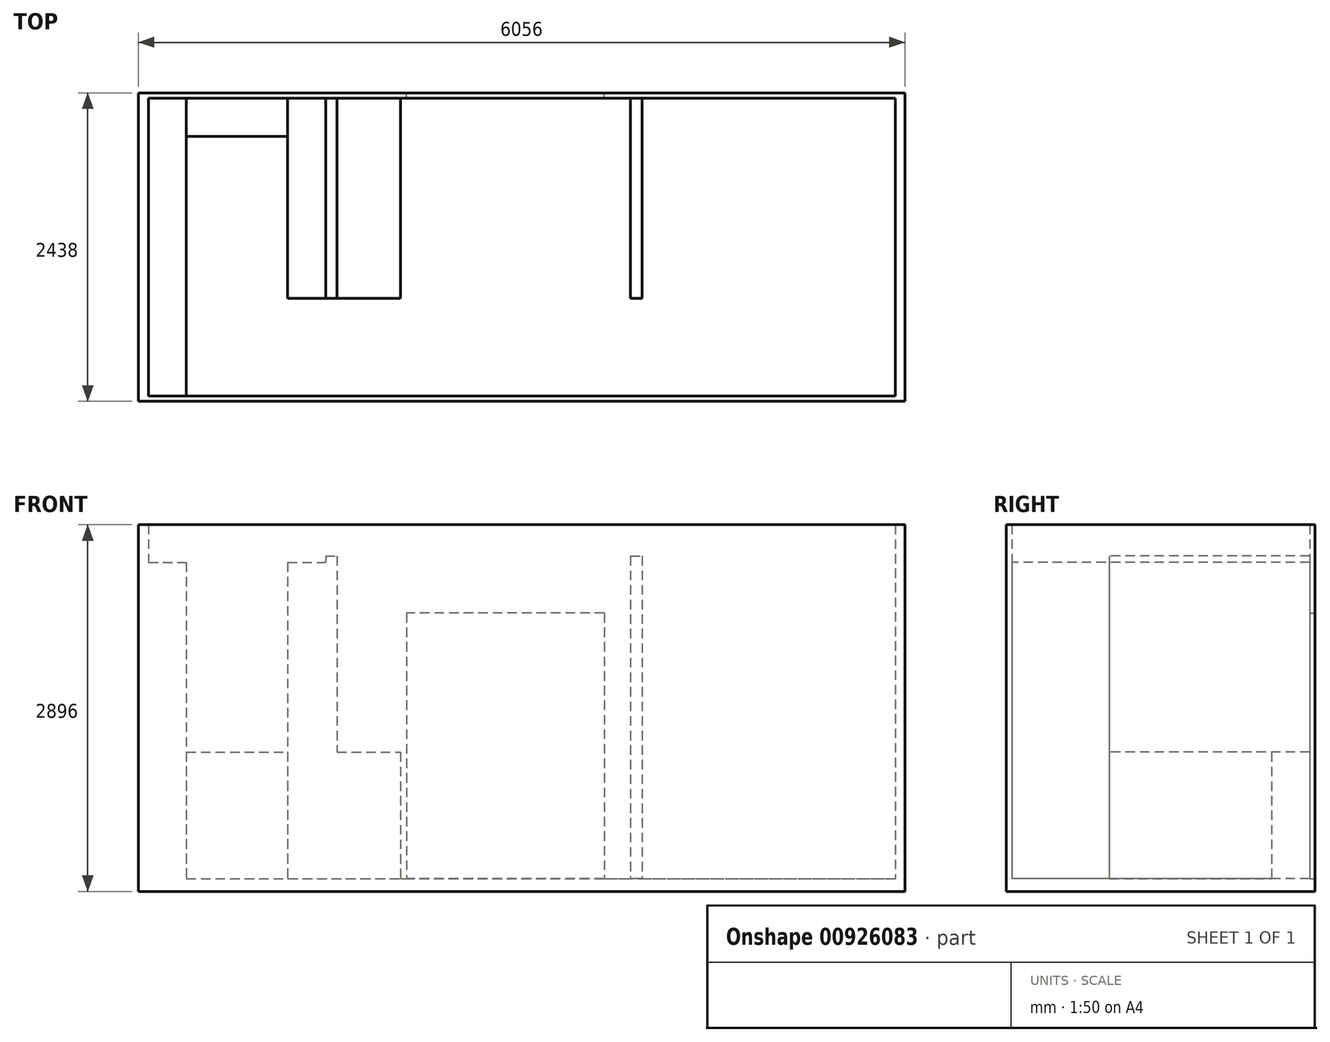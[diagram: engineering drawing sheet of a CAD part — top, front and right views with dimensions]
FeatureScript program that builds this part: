
annotation { "Feature Type Name" : "Feature", "Feature Type Description" : "" }
export const myFeature = defineFeature(function(context is Context, id is Id, definition is map)
    precondition{}
    {
        {
            var Q0;
            Q0=qCreatedBy(makeId("Top.planeOp"),FACE);
            var sketch = newSketch(context, id + "F0", { "sketchPlane" : qUnion([Q0])});
            skLineSegment(sketch, "E0.bottom", {"start": v(-2949, 1176) * mm, "end": v(2949, 1176) * mm});
            skLineSegment(sketch, "E0.top", {"start": v(-2949, -1176) * mm, "end": v(2949, -1176) * mm});
            skLineSegment(sketch, "E0.left", {"start": v(-2949, 1176) * mm, "end": v(-2949, -1176) * mm});
            skLineSegment(sketch, "E0.right", {"start": v(2949, 1176) * mm, "end": v(2949, -1176) * mm});
            skLineSegment(sketch, "E1.bottom", {"start": v(-3028, 1219) * mm, "end": v(3028, 1219) * mm});
            skLineSegment(sketch, "E1.top", {"start": v(-3028, -1219) * mm, "end": v(3028, -1219) * mm});
            skLineSegment(sketch, "E1.left", {"start": v(-3028, 1219) * mm, "end": v(-3028, -1219) * mm});
            skLineSegment(sketch, "E1.right", {"start": v(3028, 1219) * mm, "end": v(3028, -1219) * mm});
            skSolve(sketch);
        }
        {
            var Q0;
            Q0=makeQuery(id+"F0.imprint","IMPRINT",FACE,{"disambiguationData":[TD([[makeQuery(id+"F0.imprint","IMPRINT",EDGE,{"derivedFrom":sQuery(id+"F0.wireOp",EDGE,"E0.bottom")}),1.0]])]});
            extrude(context, id + "F1", {"entities" : qUnion([Q0]), "depth" : 2896 * mm, "offsetDistance" : 25 * mm});
        }
        {
            var Q0;
            Q0=makeQuery(id+"F0.imprint","IMPRINT",FACE,{"disambiguationData":[TD([[makeQuery(id+"F0.imprint","IMPRINT",EDGE,{"derivedFrom":sQuery(id+"F0.wireOp",EDGE,"E0.bottom")}),-1.0]])]});
            extrude(context, id + "F2", {"entities" : qUnion([Q0]), "operationType" : NewBodyOperationType.ADD, "depth" : 99 * mm, "offsetDistance" : 25 * mm});
        }
        {
            var Q0;
            Q0=makeQuery(id+"F2.opExtrude","CAP_FACE",FACE,{"disambiguationData":[OSD([sQuery(id+"F0.wireOp",EDGE,"E0.bottom"),sQuery(id+"F0.wireOp",EDGE,"E0.top"),sQuery(id+"F0.wireOp",EDGE,"E0.left"),sQuery(id+"F0.wireOp",EDGE,"E0.right")])],"isStart":false});
            var sketch = newSketch(context, id + "F3", { "sketchPlane" : qUnion([Q0])});
            skLineSegment(sketch, "E2.bottom", {"start": v(949, 1176) * mm, "end": v(859, 1176) * mm});
            skLineSegment(sketch, "E2.top", {"start": v(949, -406) * mm, "end": v(859, -406) * mm});
            skLineSegment(sketch, "E2.left", {"start": v(949, 1176) * mm, "end": v(949, -406) * mm});
            skLineSegment(sketch, "E2.right", {"start": v(859, 1176) * mm, "end": v(859, -406) * mm});
            skLineSegment(sketch, "E3.bottom", {"start": v(-1549, 1176) * mm, "end": v(-1459, 1176) * mm});
            skLineSegment(sketch, "E3.top", {"start": v(-1549, -406) * mm, "end": v(-1459, -406) * mm});
            skLineSegment(sketch, "E3.left", {"start": v(-1549, 1176) * mm, "end": v(-1549, -406) * mm});
            skLineSegment(sketch, "E3.right", {"start": v(-1459, 1176) * mm, "end": v(-1459, -406) * mm});
            skSolve(sketch);
        }
        {
            var Q0;
            Q0=makeQuery(id+"F3.imprint","IMPRINT",FACE,{"disambiguationData":[TD([[makeQuery(id+"F3.imprint","IMPRINT",EDGE,{"derivedFrom":sQuery(id+"F3.wireOp",EDGE,"E3.bottom")}),-1.0]])]});
            var Q1;
            Q1=makeQuery(id+"F3.imprint","IMPRINT",FACE,{"disambiguationData":[TD([[makeQuery(id+"F3.imprint","IMPRINT",EDGE,{"derivedFrom":sQuery(id+"F3.wireOp",EDGE,"E2.bottom")}),-1.0]])]});
            extrude(context, id + "F4", {"entities" : qUnion([Q0, Q1]), "operationType" : NewBodyOperationType.ADD, "depth" : 2550 * mm, "offsetDistance" : 25 * mm});
        }
        {
            var Q0;
            Q0=makeQuery(id+"F1.opExtrude","SWEPT_FACE",FACE,{"disambiguationData":[OSD([sQuery(id+"F0.wireOp",EDGE,"E1.bottom")])]});
            var sketch = newSketch(context, id + "F5", { "sketchPlane" : qUnion([Q0])});
            skLineSegment(sketch, "E4.bottom", {"start": v(-651, 2199) * mm, "end": v(909, 2199) * mm});
            skLineSegment(sketch, "E4.top", {"start": v(-651, 99) * mm, "end": v(909, 99) * mm});
            skLineSegment(sketch, "E4.left", {"start": v(-651, 2199) * mm, "end": v(-651, 99) * mm});
            skLineSegment(sketch, "E4.right", {"start": v(909, 2199) * mm, "end": v(909, 99) * mm});
            skSolve(sketch);
        }
        {
            var Q0;
            Q0=makeQuery(id+"F5.imprint","IMPRINT",FACE,{"disambiguationData":[TD([[makeQuery(id+"F5.imprint","IMPRINT",EDGE,{"derivedFrom":sQuery(id+"F5.wireOp",EDGE,"E4.bottom")}),-1.0]])]});
            extrude(context, id + "F6", {"entities" : qUnion([Q0]), "operationType" : NewBodyOperationType.REMOVE, "oppositeDirection" : true, "depth" : 49 * mm, "offsetDistance" : 25 * mm});
        }
        {
            var Q0;
            Q0=makeQuery(id+"F6.boolean.opBoolean","MERGE",FACE,{"derivedFrom":[makeQuery(id+"F2.opExtrude","CAP_FACE",FACE,{"disambiguationData":[OSD([sQuery(id+"F0.wireOp",EDGE,"E0.bottom"),sQuery(id+"F0.wireOp",EDGE,"E0.top"),sQuery(id+"F0.wireOp",EDGE,"E0.left"),sQuery(id+"F0.wireOp",EDGE,"E0.right")])],"isStart":false})],"fromTools":[makeQuery(id+"F6.opExtrude","SWEPT_FACE",FACE,{"disambiguationData":[OSD([sQuery(id+"F5.wireOp",EDGE,"E4.top")])]})]});
            var sketch = newSketch(context, id + "F7", { "sketchPlane" : qUnion([Q0])});
            skLineSegment(sketch, "E5.bottom", {"start": v(-2949, 1176) * mm, "end": v(-2649, 1176) * mm});
            skLineSegment(sketch, "E5.top", {"start": v(-2949, -1176) * mm, "end": v(-2649, -1176) * mm});
            skLineSegment(sketch, "E5.left", {"start": v(-2949, 1176) * mm, "end": v(-2949, -1176) * mm});
            skLineSegment(sketch, "E5.right", {"start": v(-2649, 1176) * mm, "end": v(-2649, -1176) * mm});
            skLineSegment(sketch, "E6.bottom", {"start": v(-1549, -406) * mm, "end": v(-1849, -406) * mm});
            skLineSegment(sketch, "E6.top", {"start": v(-1549, 1176) * mm, "end": v(-1849, 1176) * mm});
            skLineSegment(sketch, "E6.left", {"start": v(-1549, -406) * mm, "end": v(-1549, 1176) * mm});
            skLineSegment(sketch, "E6.right", {"start": v(-1849, -406) * mm, "end": v(-1849, 1176) * mm});
            skLineSegment(sketch, "E7.bottom", {"start": v(-2649, 1176) * mm, "end": v(-1849, 1176) * mm});
            skLineSegment(sketch, "E7.top", {"start": v(-2649, 876) * mm, "end": v(-1849, 876) * mm});
            skLineSegment(sketch, "E7.left", {"start": v(-2649, 1176) * mm, "end": v(-2649, 876) * mm});
            skLineSegment(sketch, "E7.right", {"start": v(-1849, 1176) * mm, "end": v(-1849, 876) * mm});
            skLineSegment(sketch, "E8.bottom", {"start": v(-1459, 1176) * mm, "end": v(-959, 1176) * mm});
            skLineSegment(sketch, "E8.top", {"start": v(-1459, -406) * mm, "end": v(-959, -406) * mm});
            skLineSegment(sketch, "E8.left", {"start": v(-1459, 1176) * mm, "end": v(-1459, -406) * mm});
            skLineSegment(sketch, "E8.right", {"start": v(-959, 1176) * mm, "end": v(-959, -406) * mm});
            skSolve(sketch);
        }
        {
            var Q0;
            {var subQ3=sQuery(id+"F7.wireOp",EDGE,"E5.bottom");Q0=makeQuery(id+"F7.imprint","IMPRINT",FACE,{"disambiguationData":[TD([[makeQuery(id+"F7.imprint","IMPRINT",EDGE,{"derivedFrom":subQ3}),-1.0]])]});}
            var Q1;
            {var subQ1=sQuery(id+"F7.wireOp",EDGE,"E6.bottom");Q1=makeQuery(id+"F7.imprint","IMPRINT",FACE,{"disambiguationData":[TD([[makeQuery(id+"F7.imprint","IMPRINT",EDGE,{"derivedFrom":subQ1}),-1.0]])]});}
            extrude(context, id + "F8", {"entities" : qUnion([Q0, Q1]), "operationType" : NewBodyOperationType.ADD, "depth" : 2500 * mm, "offsetDistance" : 25 * mm});
        }
        {
            var Q0;
            {var subQ0=sQuery(id+"F7.wireOp",EDGE,"E7.bottom");Q0=makeQuery(id+"F7.imprint","IMPRINT",FACE,{"disambiguationData":[TD([[makeQuery(id+"F7.imprint","IMPRINT",EDGE,{"derivedFrom":subQ0}),-1.0]])]});}
            var Q1;
            Q1=makeQuery(id+"F7.imprint","IMPRINT",FACE,{"disambiguationData":[TD([[makeQuery(id+"F7.imprint","IMPRINT",EDGE,{"derivedFrom":sQuery(id+"F7.wireOp",EDGE,"E8.bottom")}),-1.0]])]});
            extrude(context, id + "F9", {"entities" : qUnion([Q0, Q1]), "operationType" : NewBodyOperationType.ADD, "depth" : 1000 * mm, "offsetDistance" : 25 * mm});
        }
    });
